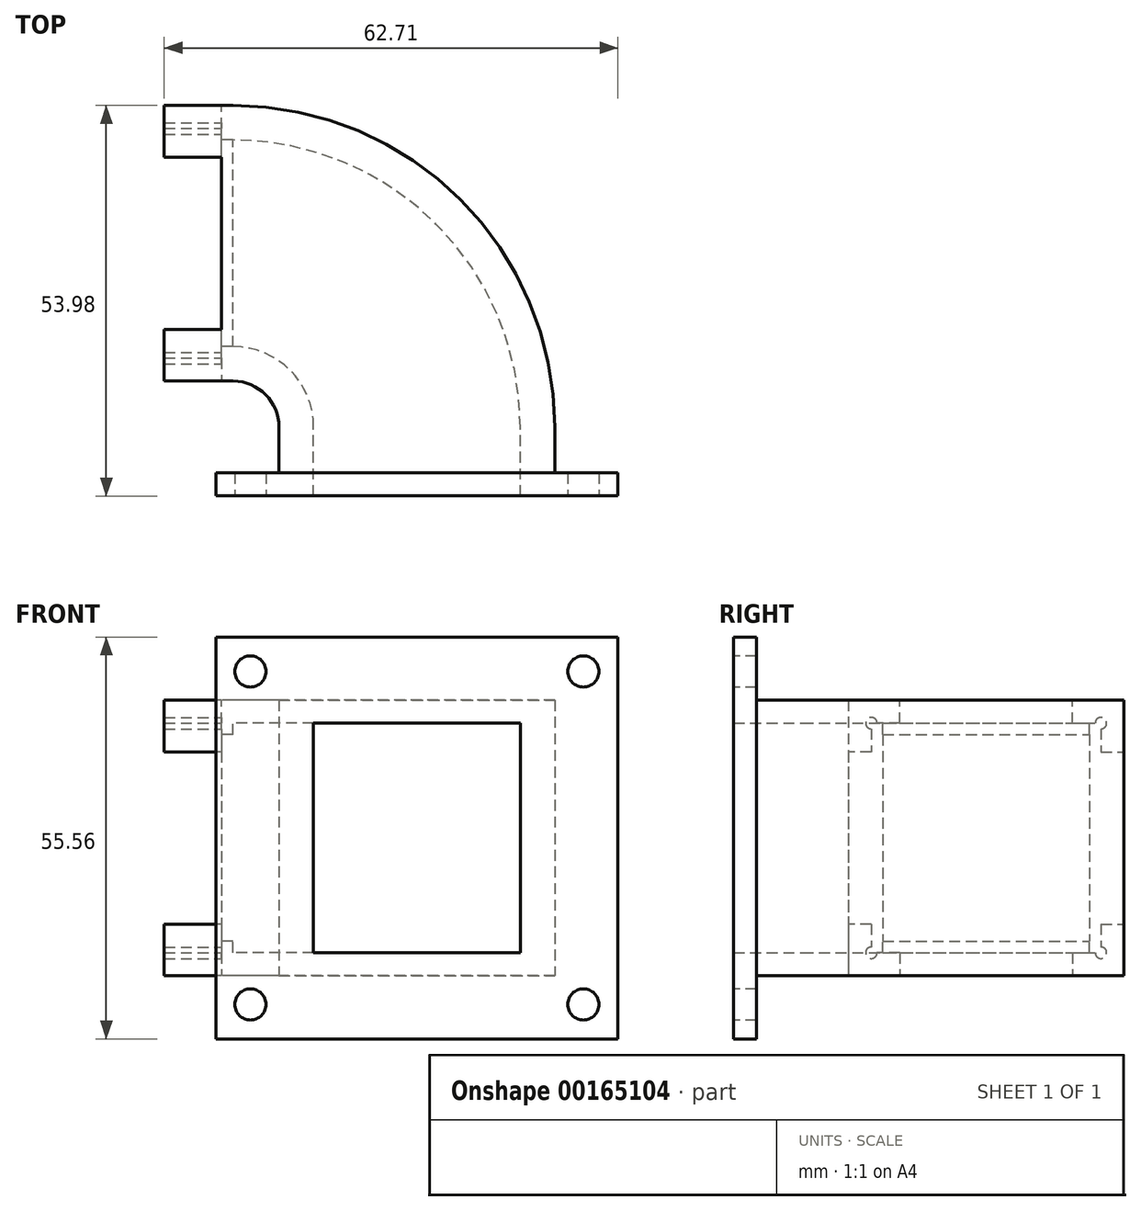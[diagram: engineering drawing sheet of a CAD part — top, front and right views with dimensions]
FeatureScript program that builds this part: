
annotation { "Feature Type Name" : "Feature", "Feature Type Description" : "" }
export const myFeature = defineFeature(function(context is Context, id is Id, definition is map)
    precondition{}
    {
        {
            var Q0;
            Q0=qCreatedBy(makeId("Top.planeOp"),FACE);
            var sketch = newSketch(context, id + "F0", { "sketchPlane" : qUnion([Q0])});
            skLineSegment(sketch, "E0.bottom", {"start": v(0, 0) * mm, "end": v(-9.53, 0) * mm});
            skLineSegment(sketch, "E0.top", {"start": v(0, -38.1) * mm, "end": v(-9.53, -38.1) * mm});
            skLineSegment(sketch, "E0.left", {"start": v(0, 0) * mm, "end": v(0, -38.1) * mm, "construction": true});
            skLineSegment(sketch, "E0.right", {"start": v(-9.53, 0) * mm, "end": v(-9.53, -38.1) * mm});
            skArc(sketch, "E1", {"start": v(44.45, -44.45) * mm, "mid": v(31.43, -13.02) * mm, "end": v(0, 0) * mm});
            skArc(sketch, "E2", {"start": v(6.35, -44.45) * mm, "mid": v(4.5, -39.96) * mm, "end": v(0, -38.1) * mm});
            skLineSegment(sketch, "E3.bottom", {"start": v(6.35, -44.45) * mm, "end": v(44.45, -44.45) * mm, "construction": true});
            skLineSegment(sketch, "E3.top", {"start": v(6.35, -53.98) * mm, "end": v(44.45, -53.98) * mm});
            skLineSegment(sketch, "E3.left", {"start": v(6.35, -44.45) * mm, "end": v(6.35, -53.98) * mm});
            skLineSegment(sketch, "E3.right", {"start": v(44.45, -44.45) * mm, "end": v(44.45, -53.98) * mm});
            skSolve(sketch);
        }
        {
            var Q0;
            Q0 = qSketchRegion(id + "F0", true);
            extrude(context, id + "F1", {"entities" : qUnion([Q0]), "depth" : 38.1 * mm});
        }
        {
            var Q0;
            Q0=makeQuery(id+"F1.opExtrude","SWEPT_FACE",FACE,{"disambiguationData":[OSD([sQuery(id+"F0.wireOp",EDGE,"E0.right")])]});
            shell(context, id + "F2", {"entities" : qUnion([Q0]), "thickness" : 3.17 * mm});
        }
        {
            var Q0;
            Q0=makeQuery(id+"F2.opShell","OFFSET_FACE",FACE,{"disambiguationData":[OSD([sQuery(id+"F0.wireOp",EDGE,"E3.top")])]});
            var Q1;
            Q1=makeQuery(id+"F1.opExtrude","SWEPT_FACE",FACE,{"disambiguationData":[OSD([sQuery(id+"F0.wireOp",EDGE,"E3.top")])]});
            extrude(context, id + "F3", {"entities" : qUnion([Q0]), "operationType" : NewBodyOperationType.REMOVE, "endBound" : BoundingType.UP_TO_SURFACE, "oppositeDirection" : true, "endBoundEntityFace" : qUnion([Q1]), "depth" : 25.4 * mm});
        }
        {
            var Q0;
            Q0=makeQuery(id+"F1.opExtrude","SWEPT_FACE",FACE,{"disambiguationData":[OSD([sQuery(id+"F0.wireOp",EDGE,"E0.right")])]});
            var sketch = newSketch(context, id + "F4", { "sketchPlane" : qUnion([Q0])});
            skLineSegment(sketch, "E4", {"start": v(3.18, 19.05) * mm, "end": v(34.92, 19.05) * mm, "construction": true});
            skLineSegment(sketch, "E5", {"start": v(19.05, 3.17) * mm, "end": v(19.05, 34.93) * mm, "construction": true});
            skLineSegment(sketch, "E6.bottom", {"start": v(3.18, 7.14) * mm, "end": v(0, 7.14) * mm});
            skLineSegment(sketch, "E6.top", {"start": v(3.18, 30.96) * mm, "end": v(0, 30.96) * mm});
            skLineSegment(sketch, "E6.left", {"start": v(3.18, 7.14) * mm, "end": v(3.18, 30.96) * mm});
            skLineSegment(sketch, "E6.right", {"start": v(0, 7.14) * mm, "end": v(0, 30.96) * mm});
            skLineSegment(sketch, "E7.bottom", {"start": v(7.14, 34.93) * mm, "end": v(30.96, 34.93) * mm});
            skLineSegment(sketch, "E7.top", {"start": v(7.14, 38.1) * mm, "end": v(30.96, 38.1) * mm});
            skLineSegment(sketch, "E7.left", {"start": v(7.14, 34.93) * mm, "end": v(7.14, 38.1) * mm});
            skLineSegment(sketch, "E7.right", {"start": v(30.96, 34.93) * mm, "end": v(30.96, 38.1) * mm});
            skLineSegment(sketch, "E8.bottom", {"start": v(34.92, 7.14) * mm, "end": v(38.1, 7.14) * mm});
            skLineSegment(sketch, "E8.top", {"start": v(34.92, 30.96) * mm, "end": v(38.1, 30.96) * mm});
            skLineSegment(sketch, "E8.left", {"start": v(34.93, 7.14) * mm, "end": v(34.92, 30.96) * mm});
            skLineSegment(sketch, "E8.right", {"start": v(38.1, 7.14) * mm, "end": v(38.1, 30.96) * mm});
            skLineSegment(sketch, "E9.bottom", {"start": v(30.96, 3.17) * mm, "end": v(7.14, 3.17) * mm});
            skLineSegment(sketch, "E9.top", {"start": v(30.96, 0) * mm, "end": v(7.14, 0) * mm});
            skLineSegment(sketch, "E9.left", {"start": v(30.96, 3.17) * mm, "end": v(30.96, 0) * mm});
            skLineSegment(sketch, "E9.right", {"start": v(7.14, 3.17) * mm, "end": v(7.14, 0) * mm});
            skCircle(sketch, "E10", {"center": v(7.14, 34.93) * mm, "radius": 0.8 * mm, "construction": true});
            skCircle(sketch, "E11", {"center": v(19.05, 19.05) * mm, "radius": 15.88 * mm, "construction": true});
            skCircle(sketch, "E12", {"center": v(7.14, 34.93) * mm, "radius": 3.97 * mm, "construction": true});
            skSolve(sketch);
        }
        {
            var Q0;
            Q0 = qSketchRegion(id + "F4", true);
            extrude(context, id + "F5", {"entities" : qUnion([Q0]), "operationType" : NewBodyOperationType.REMOVE, "oppositeDirection" : true, "depth" : 7.94 * mm});
        }
        {
            var Q0;
            Q0=makeQuery(id+"F1.opExtrude","SWEPT_FACE",FACE,{"disambiguationData":[OSD([sQuery(id+"F0.wireOp",EDGE,"E3.top")])]});
            var sketch = newSketch(context, id + "F6", { "sketchPlane" : qUnion([Q0])});
            skLineSegment(sketch, "E13", {"start": v(25.4, 34.93) * mm, "end": v(25.4, 3.17) * mm, "construction": true});
            skLineSegment(sketch, "E14.bottom", {"start": v(48.42, 42.07) * mm, "end": v(2.38, 42.07) * mm, "construction": true});
            skLineSegment(sketch, "E14.top", {"start": v(48.42, -3.97) * mm, "end": v(2.38, -3.97) * mm, "construction": true});
            skLineSegment(sketch, "E14.left", {"start": v(48.42, 42.07) * mm, "end": v(48.42, -3.97) * mm, "construction": true});
            skLineSegment(sketch, "E14.right", {"start": v(2.38, 42.07) * mm, "end": v(2.38, -3.97) * mm, "construction": true});
            skPoint(sketch, "E14.middle", {"position": v(25.4, 19.05) * mm});
            skLineSegment(sketch, "E15", {"start": v(25.4, 38.1) * mm, "end": v(25.4, 42.07) * mm, "construction": true});
            skLineSegment(sketch, "E16", {"start": v(25.4, 42.07) * mm, "end": v(25.4, 46.83) * mm, "construction": true});
            skLineSegment(sketch, "E17.bottom", {"start": v(53.18, 46.83) * mm, "end": v(-2.38, 46.83) * mm});
            skLineSegment(sketch, "E17.top", {"start": v(53.18, -8.73) * mm, "end": v(-2.38, -8.73) * mm});
            skLineSegment(sketch, "E17.left", {"start": v(53.18, 46.83) * mm, "end": v(53.18, -8.73) * mm});
            skLineSegment(sketch, "E17.right", {"start": v(-2.38, 46.83) * mm, "end": v(-2.38, -8.73) * mm});
            skCircle(sketch, "E18", {"center": v(48.42, 42.07) * mm, "radius": 2.15 * mm});
            skCircle(sketch, "E19", {"center": v(2.38, 42.07) * mm, "radius": 2.15 * mm});
            skCircle(sketch, "E20", {"center": v(48.42, -3.97) * mm, "radius": 2.15 * mm});
            skCircle(sketch, "E21", {"center": v(2.38, -3.97) * mm, "radius": 2.15 * mm});
            skLineSegment(sketch, "E22.bottom", {"start": v(9.53, 34.93) * mm, "end": v(41.27, 34.93) * mm});
            skLineSegment(sketch, "E22.top", {"start": v(9.53, 3.17) * mm, "end": v(41.27, 3.17) * mm});
            skLineSegment(sketch, "E22.left", {"start": v(9.53, 34.93) * mm, "end": v(9.53, 3.17) * mm});
            skLineSegment(sketch, "E22.right", {"start": v(41.27, 34.93) * mm, "end": v(41.27, 3.17) * mm});
            skSolve(sketch);
        }
        {
            var Q0;
            Q0 = qSketchRegion(id + "F6", true);
            extrude(context, id + "F7", {"entities" : qUnion([Q0]), "operationType" : NewBodyOperationType.ADD, "oppositeDirection" : true, "depth" : 3.17 * mm});
        }
        {
            var Q0;
            Q0=makeQuery(id+"F5.boolean.opBoolean","COPY",FACE,{"derivedFrom":makeQuery(id+"F5.opExtrude","CAP_FACE",FACE,{"disambiguationData":[OSD([sQuery(id+"F4.wireOp",EDGE,"E6.bottom"),sQuery(id+"F4.wireOp",EDGE,"E6.top"),sQuery(id+"F4.wireOp",EDGE,"E6.left"),sQuery(id+"F4.wireOp",EDGE,"E6.right")])],"isStart":false})});
            var sketch = newSketch(context, id + "F8", { "sketchPlane" : qUnion([Q0])});
            skLineSegment(sketch, "E23", {"start": v(3.18, 19.05) * mm, "end": v(34.92, 19.05) * mm, "construction": true});
            skLineSegment(sketch, "E24.bottom", {"start": v(34.92, 34.93) * mm, "end": v(3.17, 34.93) * mm});
            skLineSegment(sketch, "E24.top", {"start": v(34.92, 3.18) * mm, "end": v(3.17, 3.18) * mm});
            skLineSegment(sketch, "E24.left", {"start": v(34.92, 34.93) * mm, "end": v(34.92, 3.18) * mm});
            skLineSegment(sketch, "E24.right", {"start": v(3.17, 34.93) * mm, "end": v(3.17, 3.18) * mm});
            skPoint(sketch, "E24.middle", {"position": v(19.05, 19.05) * mm});
            skLineSegment(sketch, "E25.bottom", {"start": v(33.34, 33.34) * mm, "end": v(4.76, 33.34) * mm});
            skLineSegment(sketch, "E25.top", {"start": v(33.34, 4.76) * mm, "end": v(4.76, 4.76) * mm});
            skLineSegment(sketch, "E25.left", {"start": v(33.34, 33.34) * mm, "end": v(33.34, 4.76) * mm});
            skLineSegment(sketch, "E25.right", {"start": v(4.76, 33.34) * mm, "end": v(4.76, 4.76) * mm});
            skLineSegment(sketch, "E26", {"start": v(19.05, 33.34) * mm, "end": v(19.05, 34.93) * mm, "construction": true});
            skSolve(sketch);
        }
        {
            var Q0;
            Q0 = qSketchRegion(id + "F8", true);
            extrude(context, id + "F9", {"entities" : qUnion([Q0]), "operationType" : NewBodyOperationType.ADD, "oppositeDirection" : true, "depth" : 1.59 * mm});
        }
        {
            var Q0;
            Q0=makeQuery(id+"F9.boolean.opBoolean","MERGE",FACE,{"derivedFrom":[makeQuery(id+"F5.boolean.opBoolean","COPY",FACE,{"derivedFrom":makeQuery(id+"F5.opExtrude","CAP_FACE",FACE,{"disambiguationData":[OSD([sQuery(id+"F4.wireOp",EDGE,"E6.bottom"),sQuery(id+"F4.wireOp",EDGE,"E6.top"),sQuery(id+"F4.wireOp",EDGE,"E6.left"),sQuery(id+"F4.wireOp",EDGE,"E6.right")])],"isStart":false})}),makeQuery(id+"F5.boolean.opBoolean","COPY",FACE,{"derivedFrom":makeQuery(id+"F5.opExtrude","CAP_FACE",FACE,{"disambiguationData":[OSD([sQuery(id+"F4.wireOp",EDGE,"E7.bottom"),sQuery(id+"F4.wireOp",EDGE,"E7.top"),sQuery(id+"F4.wireOp",EDGE,"E7.left"),sQuery(id+"F4.wireOp",EDGE,"E7.right")])],"isStart":false})}),makeQuery(id+"F5.boolean.opBoolean","COPY",FACE,{"derivedFrom":makeQuery(id+"F5.opExtrude","CAP_FACE",FACE,{"disambiguationData":[OSD([sQuery(id+"F4.wireOp",EDGE,"E8.bottom"),sQuery(id+"F4.wireOp",EDGE,"E8.top"),sQuery(id+"F4.wireOp",EDGE,"E8.left"),sQuery(id+"F4.wireOp",EDGE,"E8.right")])],"isStart":false})}),makeQuery(id+"F5.boolean.opBoolean","COPY",FACE,{"derivedFrom":makeQuery(id+"F5.opExtrude","CAP_FACE",FACE,{"disambiguationData":[OSD([sQuery(id+"F4.wireOp",EDGE,"E9.bottom"),sQuery(id+"F4.wireOp",EDGE,"E9.top"),sQuery(id+"F4.wireOp",EDGE,"E9.left"),sQuery(id+"F4.wireOp",EDGE,"E9.right")])],"isStart":false})}),makeQuery(id+"F9.opExtrude","CAP_FACE",FACE,{"disambiguationData":[OSD([sQuery(id+"F8.wireOp",EDGE,"E24.bottom"),sQuery(id+"F8.wireOp",EDGE,"E24.top"),sQuery(id+"F8.wireOp",EDGE,"E24.left"),sQuery(id+"F8.wireOp",EDGE,"E24.right"),sQuery(id+"F8.wireOp",EDGE,"E25.bottom"),sQuery(id+"F8.wireOp",EDGE,"E25.top"),sQuery(id+"F8.wireOp",EDGE,"E25.left"),sQuery(id+"F8.wireOp",EDGE,"E25.right")])],"isStart":true})]});
            var sketch = newSketch(context, id + "F10", { "sketchPlane" : qUnion([Q0])});
            skCircle(sketch, "E27", {"center": v(3.17, 34.93) * mm, "radius": 0.8 * mm});
            skCircle(sketch, "E28", {"center": v(3.17, 3.17) * mm, "radius": 0.8 * mm});
            skCircle(sketch, "E29", {"center": v(34.92, 34.93) * mm, "radius": 0.8 * mm});
            skCircle(sketch, "E30", {"center": v(34.92, 3.17) * mm, "radius": 0.8 * mm});
            skSolve(sketch);
        }
        {
            var Q0;
            Q0 = qSketchRegion(id + "F10", true);
            var Q1;
            {var subQ5=sQuery(id+"F0.wireOp",EDGE,"E0.right");Q1=makeQuery(id+"F5.boolean.opBoolean","SPLIT",FACE,{"disambiguationData":[TD([makeQuery(id+"F5.opExtrude","SWEPT_FACE",FACE,{"disambiguationData":[OSD([sQuery(id+"F4.wireOp",EDGE,"E6.top")])]})])],"derivedFrom":makeQuery(id+"F1.opExtrude","SWEPT_FACE",FACE,{"disambiguationData":[OSD([subQ5])]})});}
            extrude(context, id + "F11", {"entities" : qUnion([Q0]), "operationType" : NewBodyOperationType.REMOVE, "endBound" : BoundingType.UP_TO_SURFACE, "endBoundEntityFace" : qUnion([Q1]), "depth" : 25.4 * mm});
        }
        {
            var Q0;
            Q0=makeQuery(id+"F7.boolean.opBoolean","MERGE",FACE,{"derivedFrom":[makeQuery(id+"F1.opExtrude","SWEPT_FACE",FACE,{"disambiguationData":[OSD([sQuery(id+"F0.wireOp",EDGE,"E3.top")])]}),makeQuery(id+"F7.opExtrude","CAP_FACE",FACE,{"disambiguationData":[OSD([sQuery(id+"F6.wireOp",EDGE,"E17.bottom"),sQuery(id+"F6.wireOp",EDGE,"E17.top"),sQuery(id+"F6.wireOp",EDGE,"E17.left"),sQuery(id+"F6.wireOp",EDGE,"E17.right"),sQuery(id+"F6.wireOp",EDGE,"E18"),sQuery(id+"F6.wireOp",EDGE,"E19"),sQuery(id+"F6.wireOp",EDGE,"E20"),sQuery(id+"F6.wireOp",EDGE,"E21"),sQuery(id+"F6.wireOp",EDGE,"E22.bottom"),sQuery(id+"F6.wireOp",EDGE,"E22.top"),sQuery(id+"F6.wireOp",EDGE,"E22.left"),sQuery(id+"F6.wireOp",EDGE,"E22.right")])],"isStart":true})]});
            var sketch = newSketch(context, id + "F12", { "sketchPlane" : qUnion([Q0])});
            skLineSegment(sketch, "E31.bottom", {"start": v(9.53, 3.18) * mm, "end": v(11.11, 3.18) * mm});
            skLineSegment(sketch, "E31.top", {"start": v(9.53, 34.93) * mm, "end": v(11.11, 34.93) * mm});
            skLineSegment(sketch, "E31.left", {"start": v(9.53, 3.18) * mm, "end": v(9.53, 34.93) * mm});
            skLineSegment(sketch, "E31.right", {"start": v(11.11, 3.18) * mm, "end": v(11.11, 34.93) * mm});
            skSolve(sketch);
        }
        {
            var Q0;
            Q0=makeQuery(id+"F12.imprint","IMPRINT",FACE,{"disambiguationData":[TD([[makeQuery(id+"F12.imprint","IMPRINT",EDGE,{"derivedFrom":sQuery(id+"F12.wireOp",EDGE,"E31.bottom")}),-1.0]])]});
            var Q1;
            {var subQ0=sQuery(id+"F0.wireOp",EDGE,"E3.left");var subQ1=sQuery(id+"F0.wireOp",EDGE,"E3.top");Q1=makeQuery(id+"F3.boolean.opBoolean","MERGE",EDGE,{"derivedFrom":[makeQuery(id+"F2.opShell","OFFSET_EDGE",EDGE,{"disambiguationData":[OSD([subQ0]),TDD([makeQuery(id+"F1.opExtrude","CAP_EDGE",EDGE,{"disambiguationData":[OSD([subQ0])],"isStart":false})])]})],"fromTools":[makeQuery(id+"F3.opExtrude","SWEPT_EDGE",EDGE,{"disambiguationData":[OSD([subQ1,subQ0]),TDD([makeQuery(id+"F2.opShell","OFFSET_VERTEX",VERTEX,{"disambiguationData":[OSD([subQ1,subQ0]),TDD([makeQuery(id+"F1.opExtrude","CAP_VERTEX",VERTEX,{"disambiguationData":[OSD([subQ1,subQ0])],"isStart":false})])]})])]})]});}
            var Q2;
            {var subQ0=sQuery(id+"F0.wireOp",EDGE,"E2");Q2=makeQuery(id+"F2.opShell","OFFSET_EDGE",EDGE,{"disambiguationData":[OSD([subQ0]),TDD([makeQuery(id+"F1.opExtrude","CAP_EDGE",EDGE,{"disambiguationData":[OSD([subQ0])],"isStart":false})])]});}
            sweep(context, id + "F13", {"operationType" : NewBodyOperationType.ADD, "profiles" : qUnion([Q0]), "path" : qUnion([Q1, Q2])});
        }
        {
            var Q0;
            {var subQ0=sQuery(id+"F0.wireOp",EDGE,"E3.top");Q0=makeQuery(id+"F13.boolean.opBoolean","MERGE",FACE,{"derivedFrom":[makeQuery(id+"F7.boolean.opBoolean","MERGE",FACE,{"derivedFrom":[makeQuery(id+"F1.opExtrude","SWEPT_FACE",FACE,{"disambiguationData":[OSD([subQ0])]}),makeQuery(id+"F7.opExtrude","CAP_FACE",FACE,{"disambiguationData":[OSD([sQuery(id+"F6.wireOp",EDGE,"E17.bottom"),sQuery(id+"F6.wireOp",EDGE,"E17.top"),sQuery(id+"F6.wireOp",EDGE,"E17.left"),sQuery(id+"F6.wireOp",EDGE,"E17.right"),sQuery(id+"F6.wireOp",EDGE,"E18"),sQuery(id+"F6.wireOp",EDGE,"E19"),sQuery(id+"F6.wireOp",EDGE,"E20"),sQuery(id+"F6.wireOp",EDGE,"E21"),sQuery(id+"F6.wireOp",EDGE,"E22.bottom"),sQuery(id+"F6.wireOp",EDGE,"E22.top"),sQuery(id+"F6.wireOp",EDGE,"E22.left"),sQuery(id+"F6.wireOp",EDGE,"E22.right")])],"isStart":true})]}),makeQuery(id+"F13.opSweep","CAP_FACE",FACE,{"disambiguationData":[OSD([subQ0,sQuery(id+"F0.wireOp",EDGE,"E3.left"),sQuery(id+"F12.wireOp",EDGE,"E31.bottom"),sQuery(id+"F12.wireOp",EDGE,"E31.top"),sQuery(id+"F12.wireOp",EDGE,"E31.left"),sQuery(id+"F12.wireOp",EDGE,"E31.right")])],"isStart":true})]});}
            var sketch = newSketch(context, id + "F14", { "sketchPlane" : qUnion([Q0])});
            skLineSegment(sketch, "E32.bottom", {"start": v(41.27, 3.18) * mm, "end": v(39.69, 3.18) * mm});
            skLineSegment(sketch, "E32.top", {"start": v(41.27, 34.93) * mm, "end": v(39.69, 34.93) * mm});
            skLineSegment(sketch, "E32.left", {"start": v(41.27, 3.18) * mm, "end": v(41.27, 34.93) * mm});
            skLineSegment(sketch, "E32.right", {"start": v(39.69, 3.18) * mm, "end": v(39.69, 34.93) * mm});
            skSolve(sketch);
        }
        {
            var Q0;
            Q0=makeQuery(id+"F14.imprint","IMPRINT",FACE,{"disambiguationData":[TD([[makeQuery(id+"F14.imprint","IMPRINT",EDGE,{"derivedFrom":sQuery(id+"F14.wireOp",EDGE,"E32.bottom")}),-1.0]])]});
            var Q1;
            {var subQ0=sQuery(id+"F0.wireOp",EDGE,"E3.right");var subQ1=sQuery(id+"F0.wireOp",EDGE,"E3.top");Q1=makeQuery(id+"F3.boolean.opBoolean","MERGE",EDGE,{"derivedFrom":[makeQuery(id+"F2.opShell","OFFSET_EDGE",EDGE,{"disambiguationData":[OSD([subQ0]),TDD([makeQuery(id+"F1.opExtrude","CAP_EDGE",EDGE,{"disambiguationData":[OSD([subQ0])],"isStart":false})])]})],"fromTools":[makeQuery(id+"F3.opExtrude","SWEPT_EDGE",EDGE,{"disambiguationData":[OSD([subQ1,subQ0]),TDD([makeQuery(id+"F2.opShell","OFFSET_VERTEX",VERTEX,{"disambiguationData":[OSD([subQ1,subQ0]),TDD([makeQuery(id+"F1.opExtrude","CAP_VERTEX",VERTEX,{"disambiguationData":[OSD([subQ1,subQ0])],"isStart":false})])]})])]})]});}
            var Q2;
            {var subQ0=sQuery(id+"F0.wireOp",EDGE,"E1");Q2=makeQuery(id+"F2.opShell","OFFSET_EDGE",EDGE,{"disambiguationData":[OSD([subQ0]),TDD([makeQuery(id+"F1.opExtrude","CAP_EDGE",EDGE,{"disambiguationData":[OSD([subQ0])],"isStart":false})])]});}
            sweep(context, id + "F15", {"operationType" : NewBodyOperationType.ADD, "profiles" : qUnion([Q0]), "path" : qUnion([Q1, Q2])});
        }
    });
